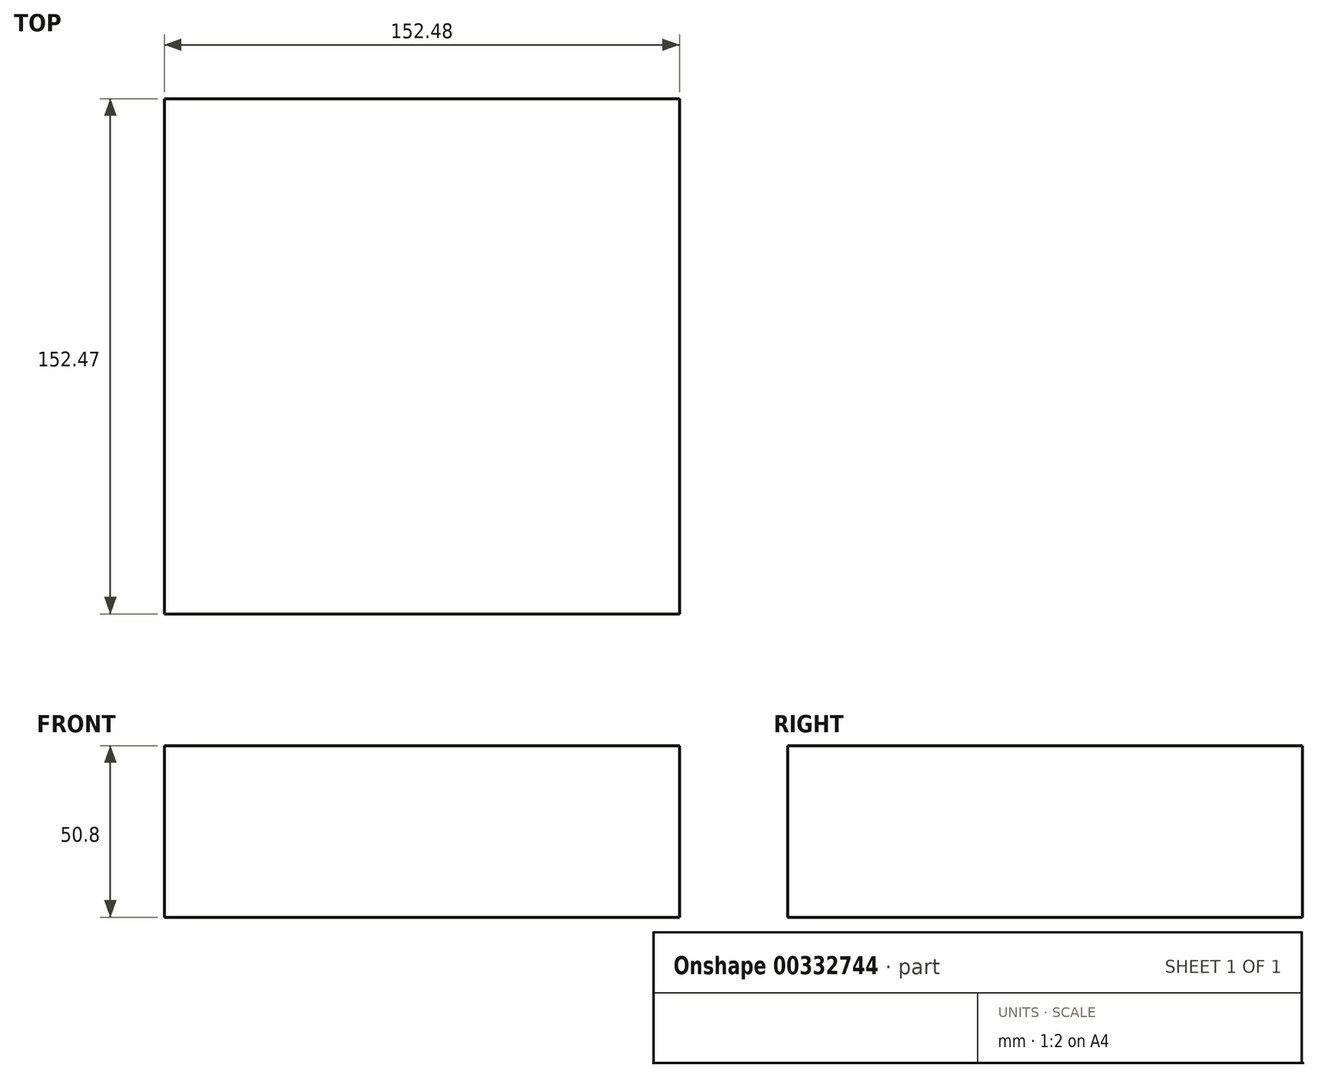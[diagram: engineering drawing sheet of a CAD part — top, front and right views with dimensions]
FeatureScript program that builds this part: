
annotation { "Feature Type Name" : "Feature", "Feature Type Description" : "" }
export const myFeature = defineFeature(function(context is Context, id is Id, definition is map)
    precondition{}
    {
        {
            var Q0;
            Q0=qCreatedBy(makeId("Top.planeOp"),FACE);
            var sketch = newSketch(context, id + "F0", { "sketchPlane" : qUnion([Q0])});
            skLineSegment(sketch, "E0.bottom", {"start": v(-76.24, 76.45) * mm, "end": v(76.24, 76.45) * mm});
            skLineSegment(sketch, "E0.top", {"start": v(-76.24, -76.02) * mm, "end": v(76.24, -76.02) * mm});
            skLineSegment(sketch, "E0.left", {"start": v(-76.24, 76.45) * mm, "end": v(-76.24, -76.02) * mm});
            skLineSegment(sketch, "E0.right", {"start": v(76.24, 76.45) * mm, "end": v(76.24, -76.02) * mm});
            skSolve(sketch);
        }
        {
            var Q0;
            Q0=makeQuery(id+"F0.imprint","IMPRINT",FACE,{"disambiguationData":[TD([[makeQuery(id+"F0.imprint","IMPRINT",EDGE,{"derivedFrom":sQuery(id+"F0.wireOp",EDGE,"E0.bottom")}),-1.0]])]});
            extrude(context, id + "F1", {"entities" : qUnion([Q0]), "depth" : 12.7 * mm});
        }
        {
            var Q0;
            Q0=makeQuery(id+"F1.opExtrude","CAP_FACE",FACE,{"disambiguationData":[OSD([sQuery(id+"F0.wireOp",EDGE,"E0.bottom"),sQuery(id+"F0.wireOp",EDGE,"E0.top"),sQuery(id+"F0.wireOp",EDGE,"E0.left"),sQuery(id+"F0.wireOp",EDGE,"E0.right")])],"isStart":false});
            extrude(context, id + "F2", {"entities" : qUnion([Q0]), "operationType" : NewBodyOperationType.ADD, "depth" : 12.7 * mm});
        }
        {
            var Q0;
            Q0=makeQuery(id+"F1.opExtrude","CAP_FACE",FACE,{"disambiguationData":[OSD([sQuery(id+"F0.wireOp",EDGE,"E0.bottom"),sQuery(id+"F0.wireOp",EDGE,"E0.top"),sQuery(id+"F0.wireOp",EDGE,"E0.left"),sQuery(id+"F0.wireOp",EDGE,"E0.right")])],"isStart":true});
            extrude(context, id + "F3", {"entities" : qUnion([Q0]), "operationType" : NewBodyOperationType.ADD, "depth" : 12.7 * mm});
        }
        {
            var Q0;
            Q0=makeQuery(id+"F3.opExtrude","CAP_FACE",FACE,{"disambiguationData":[OSD([sQuery(id+"F0.wireOp",EDGE,"E0.bottom"),sQuery(id+"F0.wireOp",EDGE,"E0.top"),sQuery(id+"F0.wireOp",EDGE,"E0.left"),sQuery(id+"F0.wireOp",EDGE,"E0.right")])],"isStart":false});
            extrude(context, id + "F4", {"entities" : qUnion([Q0]), "operationType" : NewBodyOperationType.ADD, "depth" : 12.7 * mm});
        }
    });
